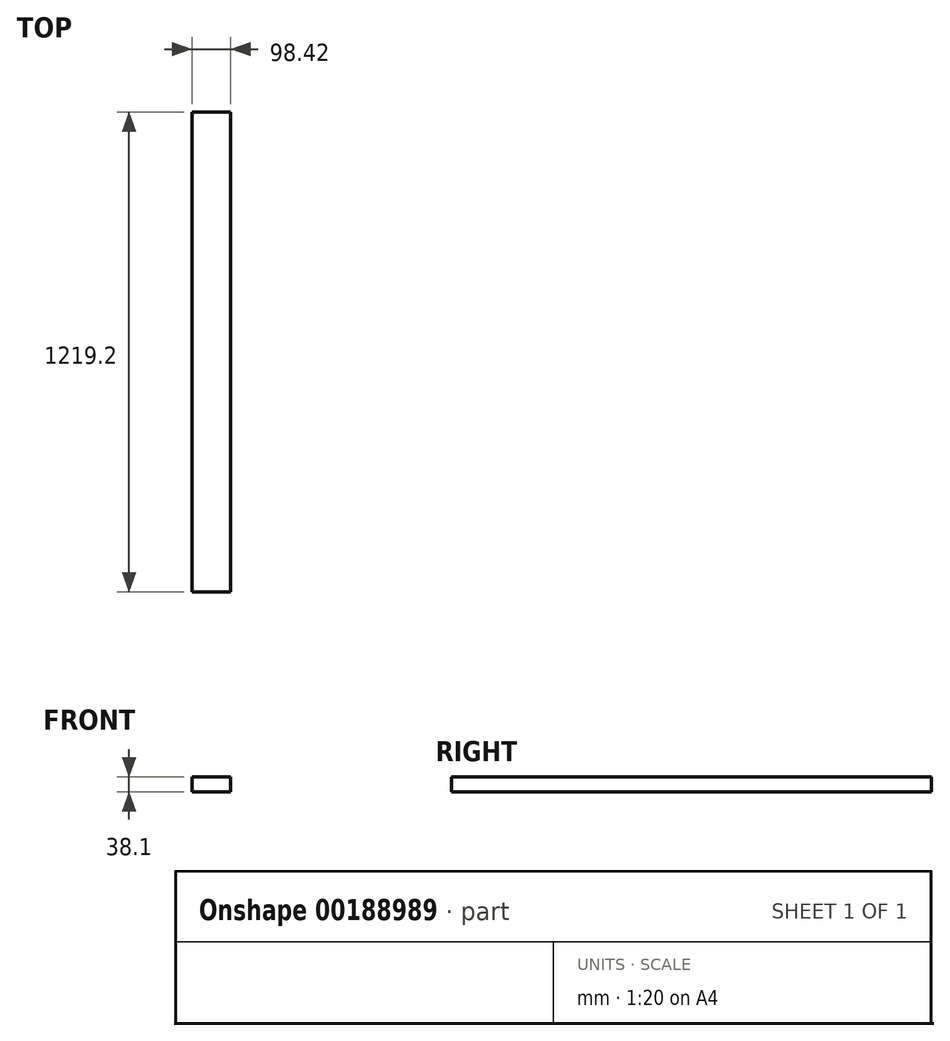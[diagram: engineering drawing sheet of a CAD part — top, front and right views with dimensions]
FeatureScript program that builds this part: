
annotation { "Feature Type Name" : "Feature", "Feature Type Description" : "" }
export const myFeature = defineFeature(function(context is Context, id is Id, definition is map)
    precondition{}
    {
        {
            var Q0;
            Q0=qCreatedBy(makeId("Front.planeOp"),FACE);
            var sketch = newSketch(context, id + "F0", { "sketchPlane" : qUnion([Q0])});
            skLineSegment(sketch, "E0.bottom", {"start": v(49.21, -19.05) * mm, "end": v(-49.21, -19.05) * mm});
            skLineSegment(sketch, "E0.top", {"start": v(49.21, 19.05) * mm, "end": v(-49.21, 19.05) * mm});
            skLineSegment(sketch, "E0.left", {"start": v(49.21, -19.05) * mm, "end": v(49.21, 19.05) * mm});
            skLineSegment(sketch, "E0.right", {"start": v(-49.21, -19.05) * mm, "end": v(-49.21, 19.05) * mm});
            skPoint(sketch, "E0.middle", {"position": v(0, 0) * mm});
            skSolve(sketch);
        }
        {
            var Q0;
            Q0 = qSketchRegion(id + "F0", true);
            extrude(context, id + "F1", {"entities" : qUnion([Q0]), "depth" : 1219.2 * mm});
        }
    });
